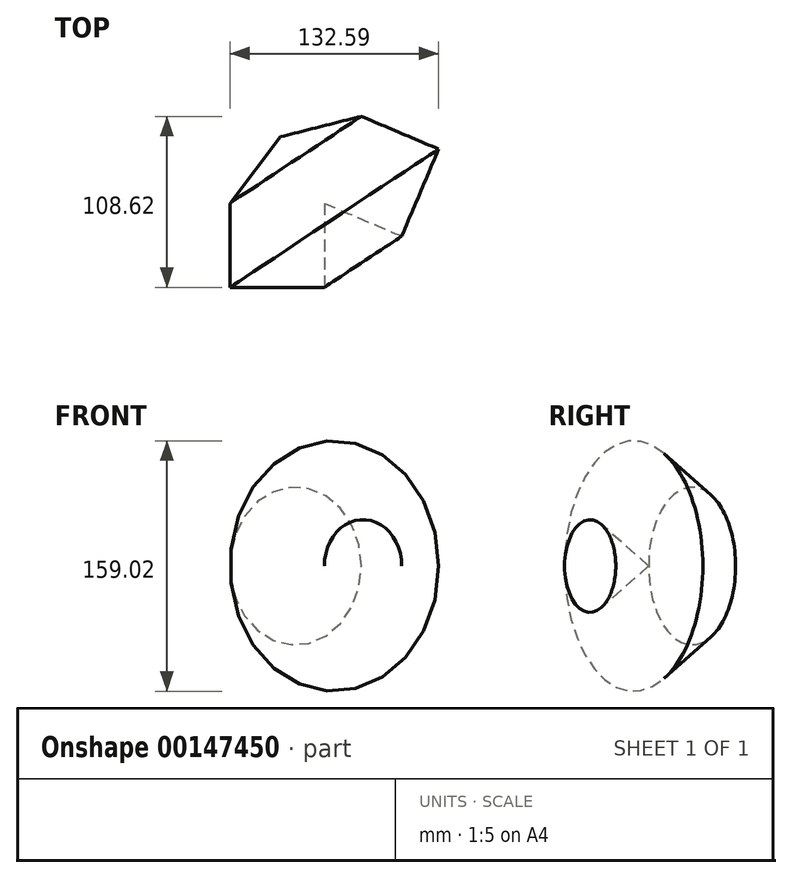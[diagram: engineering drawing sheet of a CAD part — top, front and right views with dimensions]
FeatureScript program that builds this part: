
annotation { "Feature Type Name" : "Feature", "Feature Type Description" : "" }
export const myFeature = defineFeature(function(context is Context, id is Id, definition is map)
    precondition{}
    {
        {
            var Q0;
            Q0=qCreatedBy(makeId("Top.planeOp"),FACE);
            var sketch = newSketch(context, id + "F0", { "sketchPlane" : qUnion([Q0])});
            skLineSegment(sketch, "E0", {"start": v(0, 55.82) * mm, "end": v(-32.06, 13.55) * mm});
            skLineSegment(sketch, "E1", {"start": v(-32.06, 13.55) * mm, "end": v(-32.06, -39.79) * mm});
            skLineSegment(sketch, "E2", {"start": v(-32.06, -39.79) * mm, "end": v(27.98, -39.79) * mm});
            skLineSegment(sketch, "E3", {"start": v(27.98, -39.79) * mm, "end": v(27.98, 13.55) * mm});
            skLineSegment(sketch, "E4", {"start": v(27.98, 13.55) * mm, "end": v(0, 55.82) * mm});
            skSolve(sketch);
        }
        {
            var Q0;
            Q0=makeQuery(id+"F0.imprint","IMPRINT",FACE,{"disambiguationData":[TD([[makeQuery(id+"F0.imprint","IMPRINT",EDGE,{"derivedFrom":sQuery(id+"F0.wireOp",EDGE,"E0")}),1.0]])]});
            var Q1;
            Q1=sQuery(id+"F0.wireOp",EDGE,"E4");
            revolve(context, id + "F1", {"entities" : qUnion([Q0]), "axis" : qUnion([Q1]), "revolveType" : RevolveType.FULL});
        }
    });
